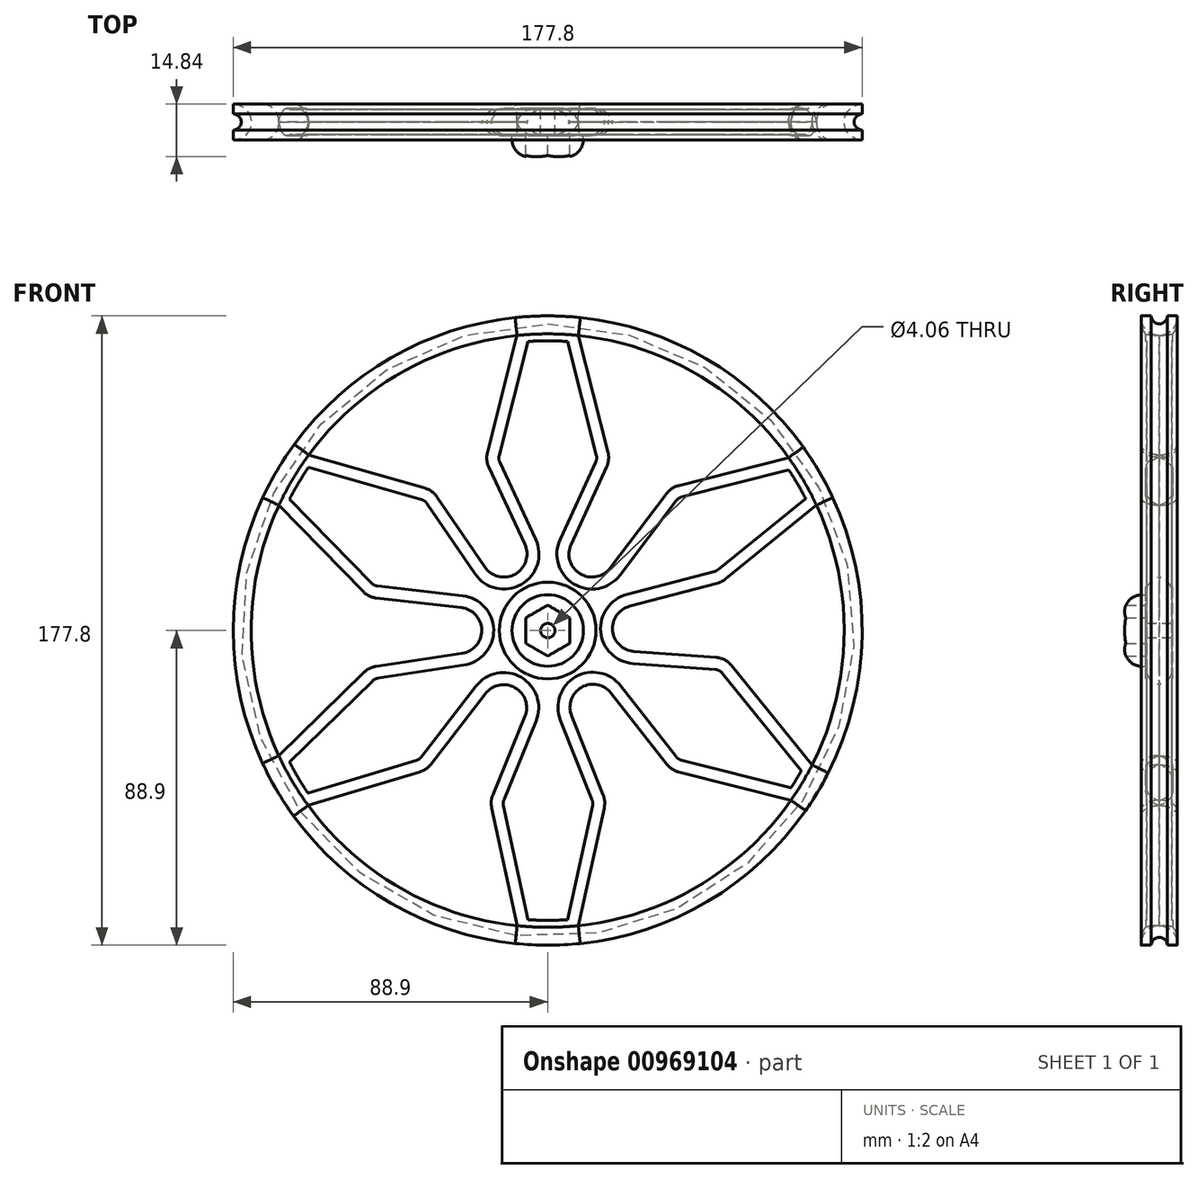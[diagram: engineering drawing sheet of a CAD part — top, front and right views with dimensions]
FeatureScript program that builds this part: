
annotation { "Feature Type Name" : "Feature", "Feature Type Description" : "" }
export const myFeature = defineFeature(function(context is Context, id is Id, definition is map)
    precondition{}
    {
        {
            var Q0;
            Q0=qCreatedBy(makeId("Top.planeOp"),FACE);
            var sketch = newSketch(context, id + "F0", { "sketchPlane" : qUnion([Q0])});
            skLineSegment(sketch, "E0", {"start": v(83.82, 0) * mm, "end": v(83.82, -5.08) * mm});
            skLineSegment(sketch, "E1", {"start": v(83.82, 0) * mm, "end": v(83.82, 5.08) * mm});
            skLineSegment(sketch, "E2", {"start": v(83.82, 5.08) * mm, "end": v(88.9, 5.08) * mm});
            skLineSegment(sketch, "E3", {"start": v(88.9, 5.08) * mm, "end": v(83.82, 5.08) * mm});
            skLineSegment(sketch, "E4", {"start": v(83.82, -5.08) * mm, "end": v(88.9, -5.08) * mm});
            skPoint(sketch, "E5.positionSnap0", {"position": v(83.82, 2.54) * mm});
            skPoint(sketch, "E6.positionSnap0", {"position": v(83.82, -2.54) * mm});
            skLineSegment(sketch, "E7", {"start": v(88.9, 3.88) * mm, "end": v(88.9, 5.08) * mm});
            skLineSegment(sketch, "E8", {"start": v(88.9, -5.08) * mm, "end": v(88.9, -3.83) * mm});
            skLineSegment(sketch, "E9", {"start": v(0, 0) * mm, "end": v(0, 19.3) * mm});
            skLineSegment(sketch, "E10", {"start": v(0, 19.3) * mm, "end": v(0, 0) * mm});
            skLineSegment(sketch, "E11", {"start": v(0, -18.69) * mm, "end": v(0, -1.26) * mm});
            skArc(sketch, "E12", {"start": v(88.9, 2.3) * mm, "mid": v(86.64, 0.03) * mm, "end": v(88.9, -2.25) * mm});
            skLineSegment(sketch, "E13", {"start": v(88.9, 2.3) * mm, "end": v(88.9, 3.88) * mm});
            skLineSegment(sketch, "E14", {"start": v(88.9, -2.25) * mm, "end": v(88.9, -3.83) * mm});
            skSolve(sketch);
        }
        {
            var Q0;
            Q0=makeQuery(id+"F0.imprint","IMPRINT",FACE,{"disambiguationData":[TD([[makeQuery(id+"F0.imprint","IMPRINT",EDGE,{"derivedFrom":sQuery(id+"F0.wireOp",EDGE,"E0")}),1.0]])]});
            var Q1;
            Q1=sQuery(id+"F0.wireOp",EDGE,"E11");
            var Q2;
            Q2=sQuery(id+"F0.wireOp",EDGE,"4J2hV2uY-nMCx-U5Xb-nDJS-bzSXFnuGIXOy");
            var Q3;
            Q3=sQuery(id+"F0.wireOp",EDGE,"E4");
            var Q4;
            Q4=sQuery(id+"F0.wireOp",EDGE,"E3");
            var Q5;
            Q5=sQuery(id+"F0.wireOp",EDGE,"E1");
            var Q6;
            Q6=sQuery(id+"F0.wireOp",EDGE,"E0");
            var Q7;
            Q7=sQuery(id+"F0.wireOp",EDGE,"E10");
            revolve(context, id + "F1", {"surfaceOperationType" : NewSurfaceOperationType.NEW, "entities" : qUnion([Q0]), "surfaceEntities" : qUnion([Q1, Q2, Q3, Q4, Q5, Q6]), "axis" : qUnion([Q7]), "revolveType" : RevolveType.FULL});
        }
        {
            var Q0;
            Q0=qCreatedBy(makeId("Front.planeOp"),FACE);
            var sketch = newSketch(context, id + "F2", { "sketchPlane" : qUnion([Q0])});
            skCircle(sketch, "E15", {"center": v(0, 0) * mm, "radius": 10.1 * mm});
            skLineSegment(sketch, "E16", {"start": v(-24.46, 6.34) * mm, "end": v(-48.48, 9.05) * mm});
            skLineSegment(sketch, "E17", {"start": v(-17.62, 18.03) * mm, "end": v(-31.2, 37.89) * mm});
            skLineSegment(sketch, "E18", {"start": v(6.74, 24.3) * mm, "end": v(16.82, 46.17) * mm});
            skLineSegment(sketch, "E19", {"start": v(-6.62, 24.3) * mm, "end": v(-16.8, 46.11) * mm});
            skLineSegment(sketch, "E20", {"start": v(17.57, 17.8) * mm, "end": v(33.5, 38.84) * mm});
            skLineSegment(sketch, "E21", {"start": v(23.23, 6.73) * mm, "end": v(48.04, 13.25) * mm});
            skLineSegment(sketch, "E22", {"start": v(24.38, -5.75) * mm, "end": v(47.6, -7.42) * mm});
            skLineSegment(sketch, "E23", {"start": v(17.82, -17.77) * mm, "end": v(33.5, -37.84) * mm});
            skLineSegment(sketch, "E24", {"start": v(6.92, -24.03) * mm, "end": v(15.83, -46.4) * mm});
            skLineSegment(sketch, "E25", {"start": v(-15.65, -46.4) * mm, "end": v(-6.58, -24.2) * mm});
            skLineSegment(sketch, "E26", {"start": v(-32.88, -37.86) * mm, "end": v(-17.48, -17.92) * mm});
            skLineSegment(sketch, "E27", {"start": v(-48.58, -9.96) * mm, "end": v(-24.22, -6.25) * mm});
            skCircle(sketch, "E28", {"center": v(0, 0) * mm, "radius": 85.43 * mm});
            skLineSegment(sketch, "E29", {"start": v(-17.2, 50.35) * mm, "end": v(-8.43, 85.01) * mm});
            skLineSegment(sketch, "E30", {"start": v(17.2, 50.39) * mm, "end": v(8.43, 85.01) * mm});
            skLineSegment(sketch, "E31", {"start": v(37, 41.16) * mm, "end": v(69.67, 49.44) * mm});
            skLineSegment(sketch, "E32", {"start": v(36.95, -40.08) * mm, "end": v(70.32, -48.51) * mm});
            skLineSegment(sketch, "E33", {"start": v(-34.7, 40.4) * mm, "end": v(-69.1, 50.24) * mm});
            skLineSegment(sketch, "E34", {"start": v(-52.3, 10.93) * mm, "end": v(-77.25, 36.47) * mm});
            skLineSegment(sketch, "E35", {"start": v(-52.06, -11.7) * mm, "end": v(-77.29, -36.4) * mm});
            skLineSegment(sketch, "E36", {"start": v(-36.08, -40.06) * mm, "end": v(-69.26, -50.02) * mm});
            skLineSegment(sketch, "E37", {"start": v(-15.98, -50.13) * mm, "end": v(-8.46, -85.01) * mm});
            skLineSegment(sketch, "E38", {"start": v(16.13, -50.11) * mm, "end": v(8.46, -85.01) * mm});
            skLineSegment(sketch, "E39", {"start": v(50.42, 14.47) * mm, "end": v(77.33, 36.32) * mm});
            skLineSegment(sketch, "E40", {"start": v(52.07, -9.75) * mm, "end": v(77.33, -40.86) * mm});
            skLineSegment(sketch, "E41", {"start": v(77.66, -35.6) * mm, "end": v(77.33, -40.86) * mm});
            skPoint(sketch, "E42.visualSharp", {"position": v(-50.73, 9.3) * mm});
            skArc(sketch, "E42.filletArc", {"start": v(-52.3, 10.93) * mm, "mid": v(-50.56, 9.66) * mm, "end": v(-48.48, 9.05) * mm});
            skPoint(sketch, "E43.visualSharp", {"position": v(-32.5, 39.78) * mm});
            skArc(sketch, "E43.filletArc", {"start": v(-31.2, 37.89) * mm, "mid": v(-32.73, 39.45) * mm, "end": v(-34.7, 40.4) * mm});
            skPoint(sketch, "E44.visualSharp", {"position": v(-50.6, -10.27) * mm});
            skArc(sketch, "E44.filletArc", {"start": v(-48.58, -9.96) * mm, "mid": v(-50.46, -10.55) * mm, "end": v(-52.06, -11.7) * mm});
            skPoint(sketch, "E45.visualSharp", {"position": v(-34.12, -39.47) * mm});
            skArc(sketch, "E45.filletArc", {"start": v(-36.08, -40.06) * mm, "mid": v(-34.3, -39.2) * mm, "end": v(-32.88, -37.86) * mm});
            skPoint(sketch, "E46.visualSharp", {"position": v(-17.75, 48.16) * mm});
            skArc(sketch, "E46.filletArc", {"start": v(-17.2, 50.35) * mm, "mid": v(-17.36, 48.2) * mm, "end": v(-16.8, 46.11) * mm});
            skPoint(sketch, "E47.visualSharp", {"position": v(17.75, 48.21) * mm});
            skArc(sketch, "E47.filletArc", {"start": v(16.82, 46.17) * mm, "mid": v(17.37, 48.25) * mm, "end": v(17.2, 50.39) * mm});
            skPoint(sketch, "E48.visualSharp", {"position": v(34.84, 40.61) * mm});
            skArc(sketch, "E48.filletArc", {"start": v(37, 41.16) * mm, "mid": v(35.05, 40.3) * mm, "end": v(33.5, 38.84) * mm});
            skPoint(sketch, "E49.visualSharp", {"position": v(49.36, 13.6) * mm});
            skArc(sketch, "E49.filletArc", {"start": v(48.04, 13.25) * mm, "mid": v(49.3, 13.73) * mm, "end": v(50.42, 14.47) * mm});
            skPoint(sketch, "E50.visualSharp", {"position": v(50.34, -7.62) * mm});
            skArc(sketch, "E50.filletArc", {"start": v(52.07, -9.75) * mm, "mid": v(50.07, -8.13) * mm, "end": v(47.6, -7.42) * mm});
            skPoint(sketch, "E51.visualSharp", {"position": v(34.84, -39.55) * mm});
            skArc(sketch, "E51.filletArc", {"start": v(33.5, -37.84) * mm, "mid": v(35.04, -39.25) * mm, "end": v(36.95, -40.08) * mm});
            skPoint(sketch, "E52.visualSharp", {"position": v(16.55, -48.21) * mm});
            skArc(sketch, "E52.filletArc", {"start": v(16.13, -50.11) * mm, "mid": v(16.26, -48.23) * mm, "end": v(15.83, -46.4) * mm});
            skPoint(sketch, "E53.visualSharp", {"position": v(-16.4, -48.21) * mm});
            skArc(sketch, "E53.filletArc", {"start": v(-15.65, -46.4) * mm, "mid": v(-16.1, -48.24) * mm, "end": v(-15.98, -50.13) * mm});
            skPoint(sketch, "E54.endSnap0", {"position": v(25.3, 7.3) * mm});
            skArc(sketch, "E55.filletArc", {"start": v(-6.58, -24.2) * mm, "mid": v(-9.28, -16.3) * mm, "end": v(-17.48, -17.92) * mm});
            skArc(sketch, "E56.filletArc", {"start": v(17.82, -17.77) * mm, "mid": v(9.66, -16.18) * mm, "end": v(6.92, -24.03) * mm});
            skArc(sketch, "E57.filletArc", {"start": v(23.23, 6.73) * mm, "mid": v(18.52, 0) * mm, "end": v(24.38, -5.75) * mm});
            skArc(sketch, "E58.filletArc", {"start": v(6.74, 24.3) * mm, "mid": v(9.25, 16.2) * mm, "end": v(17.57, 17.8) * mm});
            skArc(sketch, "E59.filletArc", {"start": v(-17.62, 18.03) * mm, "mid": v(-9.23, 16.1) * mm, "end": v(-6.62, 24.3) * mm});
            skArc(sketch, "E60.filletArc", {"start": v(-24.22, -6.25) * mm, "mid": v(-18.82, 0.15) * mm, "end": v(-24.46, 6.34) * mm});
            skPoint(sketch, "E61.startSnap0", {"position": v(18.52, 0) * mm});
            skCircle(sketch, "E62", {"center": v(0, 0) * mm, "radius": 2.03 * mm});
            skLineSegment(sketch, "E63.0", {"start": v(0, -7.19) * mm, "end": v(-6.22, -3.6) * mm});
            skLineSegment(sketch, "E63.1", {"start": v(-6.22, -3.6) * mm, "end": v(-6.22, 3.6) * mm});
            skLineSegment(sketch, "E63.2", {"start": v(-6.22, 3.6) * mm, "end": v(0, 7.19) * mm});
            skLineSegment(sketch, "E63.3", {"start": v(0, 7.19) * mm, "end": v(6.22, 3.6) * mm});
            skLineSegment(sketch, "E63.4", {"start": v(6.22, 3.6) * mm, "end": v(6.22, -3.6) * mm});
            skLineSegment(sketch, "E63.5", {"start": v(6.22, -3.6) * mm, "end": v(0, -7.19) * mm});
            skSolve(sketch);
        }
        {
            var Q0;
            Q0=makeQuery(id+"F2.imprint","IMPRINT",FACE,{"disambiguationData":[TD([[makeQuery(id+"F2.imprint","IMPRINT",EDGE,{"derivedFrom":sQuery(id+"F2.wireOp",EDGE,"E18")}),1.0]])]});
            var Q1;
            Q1=makeQuery(id+"F2.imprint","IMPRINT",FACE,{"disambiguationData":[TD([[makeQuery(id+"F2.imprint","IMPRINT",EDGE,{"derivedFrom":sQuery(id+"F2.wireOp",EDGE,"E20")}),-1.0]])]});
            var Q2;
            Q2=makeQuery(id+"F2.imprint","IMPRINT",FACE,{"disambiguationData":[TD([[makeQuery(id+"F2.imprint","IMPRINT",EDGE,{"derivedFrom":sQuery(id+"F2.wireOp",EDGE,"E22")}),-1.0]])]});
            var Q3;
            Q3=makeQuery(id+"F2.imprint","IMPRINT",FACE,{"disambiguationData":[TD([[makeQuery(id+"F2.imprint","IMPRINT",EDGE,{"derivedFrom":sQuery(id+"F2.wireOp",EDGE,"E24")}),-1.0]])]});
            var Q4;
            Q4=makeQuery(id+"F2.imprint","IMPRINT",FACE,{"disambiguationData":[TD([[makeQuery(id+"F2.imprint","IMPRINT",EDGE,{"derivedFrom":sQuery(id+"F2.wireOp",EDGE,"E26")}),1.0]])]});
            var Q5;
            Q5=makeQuery(id+"F2.imprint","IMPRINT",FACE,{"disambiguationData":[TD([[makeQuery(id+"F2.imprint","IMPRINT",EDGE,{"derivedFrom":sQuery(id+"F2.wireOp",EDGE,"E16")}),-1.0]])]});
            var Q6;
            Q6=makeQuery(id+"F2.imprint","IMPRINT",FACE,{"disambiguationData":[TD([[makeQuery(id+"F2.imprint","IMPRINT",EDGE,{"derivedFrom":sQuery(id+"F2.wireOp",EDGE,"c844d40d-d56d-44c7-8cb0-b91d600c20de.0")}),-1.0]])]});
            var Q7;
            Q7=makeQuery(id+"F2.imprint","IMPRINT",FACE,{"disambiguationData":[TD([[makeQuery(id+"F2.imprint","IMPRINT",EDGE,{"derivedFrom":sQuery(id+"F2.wireOp",EDGE,"E62")}),-1.0]])]});
            extrude(context, id + "F3", {"entities" : qUnion([Q0, Q1, Q2, Q3, Q4, Q5, Q6, Q7]), "depth" : 3.8 * mm, "offsetDistance" : 25.4 * mm});
        }
        {
            var Q0;
            Q0=makeQuery(id+"F3.opExtrude","CAP_FACE",FACE,{"disambiguationData":[OSD([sQuery(id+"F2.wireOp",EDGE,"E16"),sQuery(id+"F2.wireOp",EDGE,"E17"),sQuery(id+"F2.wireOp",EDGE,"E28"),sQuery(id+"F2.wireOp",EDGE,"E33"),sQuery(id+"F2.wireOp",EDGE,"E34"),sQuery(id+"F2.wireOp",EDGE,"E42.filletArc"),sQuery(id+"F2.wireOp",EDGE,"E43.filletArc")])],"isStart":false});
            var Q1;
            Q1=makeQuery(id+"F3.opExtrude","CAP_FACE",FACE,{"disambiguationData":[OSD([sQuery(id+"F2.wireOp",EDGE,"E18"),sQuery(id+"F2.wireOp",EDGE,"E19"),sQuery(id+"F2.wireOp",EDGE,"E28"),sQuery(id+"F2.wireOp",EDGE,"E29"),sQuery(id+"F2.wireOp",EDGE,"E30"),sQuery(id+"F2.wireOp",EDGE,"E46.filletArc"),sQuery(id+"F2.wireOp",EDGE,"E47.filletArc")])],"isStart":false});
            var Q2;
            Q2=makeQuery(id+"F3.opExtrude","CAP_FACE",FACE,{"disambiguationData":[OSD([sQuery(id+"F2.wireOp",EDGE,"E20"),sQuery(id+"F2.wireOp",EDGE,"E21"),sQuery(id+"F2.wireOp",EDGE,"E28"),sQuery(id+"F2.wireOp",EDGE,"E31"),sQuery(id+"F2.wireOp",EDGE,"E39"),sQuery(id+"F2.wireOp",EDGE,"E48.filletArc"),sQuery(id+"F2.wireOp",EDGE,"E49.filletArc")])],"isStart":false});
            var Q3;
            Q3=makeQuery(id+"F3.opExtrude","CAP_FACE",FACE,{"disambiguationData":[OSD([sQuery(id+"F2.wireOp",EDGE,"E22"),sQuery(id+"F2.wireOp",EDGE,"E23"),sQuery(id+"F2.wireOp",EDGE,"E28"),sQuery(id+"F2.wireOp",EDGE,"E32"),sQuery(id+"F2.wireOp",EDGE,"E40"),sQuery(id+"F2.wireOp",EDGE,"E41"),sQuery(id+"F2.wireOp",EDGE,"E50.filletArc"),sQuery(id+"F2.wireOp",EDGE,"E51.filletArc")])],"isStart":false});
            var Q4;
            Q4=makeQuery(id+"F3.opExtrude","CAP_FACE",FACE,{"disambiguationData":[OSD([sQuery(id+"F2.wireOp",EDGE,"E24"),sQuery(id+"F2.wireOp",EDGE,"E25"),sQuery(id+"F2.wireOp",EDGE,"E28"),sQuery(id+"F2.wireOp",EDGE,"E37"),sQuery(id+"F2.wireOp",EDGE,"E38"),sQuery(id+"F2.wireOp",EDGE,"E52.filletArc"),sQuery(id+"F2.wireOp",EDGE,"E53.filletArc")])],"isStart":false});
            var Q5;
            Q5=makeQuery(id+"F3.opExtrude","CAP_FACE",FACE,{"disambiguationData":[OSD([sQuery(id+"F2.wireOp",EDGE,"E26"),sQuery(id+"F2.wireOp",EDGE,"E27"),sQuery(id+"F2.wireOp",EDGE,"E28"),sQuery(id+"F2.wireOp",EDGE,"E35"),sQuery(id+"F2.wireOp",EDGE,"E36"),sQuery(id+"F2.wireOp",EDGE,"E44.filletArc"),sQuery(id+"F2.wireOp",EDGE,"E45.filletArc")])],"isStart":false});
            shell(context, id + "F4", {"entities" : qUnion([Q0, Q1, Q2, Q3, Q4, Q5]), "thickness" : 3.56 * mm});
        }
        {
            var Q0;
            Q0=makeQuery(id+"F3.opExtrude","SWEPT_BODY",BODY,{"disambiguationData":[OSD([sQuery(id+"F2.wireOp",EDGE,"E20"),sQuery(id+"F2.wireOp",EDGE,"E21"),sQuery(id+"F2.wireOp",EDGE,"E28"),sQuery(id+"F2.wireOp",EDGE,"E31"),sQuery(id+"F2.wireOp",EDGE,"E39")])]});
            var Q1;
            Q1=makeQuery(id+"F3.opExtrude","SWEPT_BODY",BODY,{"disambiguationData":[OSD([sQuery(id+"F2.wireOp",EDGE,"E22"),sQuery(id+"F2.wireOp",EDGE,"E23"),sQuery(id+"F2.wireOp",EDGE,"E28"),sQuery(id+"F2.wireOp",EDGE,"E32"),sQuery(id+"F2.wireOp",EDGE,"E40"),sQuery(id+"F2.wireOp",EDGE,"E41")])]});
            var Q2;
            Q2=makeQuery(id+"F3.opExtrude","SWEPT_BODY",BODY,{"disambiguationData":[OSD([sQuery(id+"F2.wireOp",EDGE,"E24"),sQuery(id+"F2.wireOp",EDGE,"E25"),sQuery(id+"F2.wireOp",EDGE,"E28"),sQuery(id+"F2.wireOp",EDGE,"E37"),sQuery(id+"F2.wireOp",EDGE,"E38")])]});
            var Q3;
            Q3=makeQuery(id+"F3.opExtrude","SWEPT_BODY",BODY,{"disambiguationData":[OSD([sQuery(id+"F2.wireOp",EDGE,"E26"),sQuery(id+"F2.wireOp",EDGE,"E27"),sQuery(id+"F2.wireOp",EDGE,"E28"),sQuery(id+"F2.wireOp",EDGE,"E35"),sQuery(id+"F2.wireOp",EDGE,"E36")])]});
            var Q4;
            Q4=makeQuery(id+"F3.opExtrude","SWEPT_BODY",BODY,{"disambiguationData":[OSD([sQuery(id+"F2.wireOp",EDGE,"c844d40d-d56d-44c7-8cb0-b91d600c20de.0"),sQuery(id+"F2.wireOp",EDGE,"c844d40d-d56d-44c7-8cb0-b91d600c20de.1"),sQuery(id+"F2.wireOp",EDGE,"c844d40d-d56d-44c7-8cb0-b91d600c20de.2"),sQuery(id+"F2.wireOp",EDGE,"c844d40d-d56d-44c7-8cb0-b91d600c20de.3"),sQuery(id+"F2.wireOp",EDGE,"c844d40d-d56d-44c7-8cb0-b91d600c20de.4"),sQuery(id+"F2.wireOp",EDGE,"c844d40d-d56d-44c7-8cb0-b91d600c20de.5")])]});
            var Q5;
            Q5=makeQuery(id+"F3.opExtrude","SWEPT_BODY",BODY,{"disambiguationData":[OSD([sQuery(id+"F2.wireOp",EDGE,"E16"),sQuery(id+"F2.wireOp",EDGE,"E17"),sQuery(id+"F2.wireOp",EDGE,"E28"),sQuery(id+"F2.wireOp",EDGE,"E33"),sQuery(id+"F2.wireOp",EDGE,"E34")])]});
            var Q6;
            Q6=makeQuery(id+"F3.opExtrude","SWEPT_BODY",BODY,{"disambiguationData":[OSD([sQuery(id+"F2.wireOp",EDGE,"E18"),sQuery(id+"F2.wireOp",EDGE,"E19"),sQuery(id+"F2.wireOp",EDGE,"E28"),sQuery(id+"F2.wireOp",EDGE,"E29"),sQuery(id+"F2.wireOp",EDGE,"E30")])]});
            var Q7;
            Q7=makeQuery(id+"FEBJNoevQ1nLVfz_7.opExtrude","SWEPT_BODY",BODY,{"disambiguationData":[OSD([sQuery(id+"F2.wireOp",EDGE,"c844d40d-d56d-44c7-8cb0-b91d600c20de.0"),sQuery(id+"F2.wireOp",EDGE,"c844d40d-d56d-44c7-8cb0-b91d600c20de.1"),sQuery(id+"F2.wireOp",EDGE,"c844d40d-d56d-44c7-8cb0-b91d600c20de.2"),sQuery(id+"F2.wireOp",EDGE,"c844d40d-d56d-44c7-8cb0-b91d600c20de.3"),sQuery(id+"F2.wireOp",EDGE,"c844d40d-d56d-44c7-8cb0-b91d600c20de.4"),sQuery(id+"F2.wireOp",EDGE,"c844d40d-d56d-44c7-8cb0-b91d600c20de.5")])]});
            var Q8;
            Q8=qCreatedBy(makeId("Front.planeOp"),FACE);
            mirror(context, id + "F5", {"entities" : qUnion([Q0, Q1, Q2, Q3, Q4, Q5, Q6, Q7]), "mirrorPlane" : qUnion([Q8])});
        }
        {
            var Q0;
            Q0=makeQuery(id+"F2.imprint","IMPRINT",FACE,{"disambiguationData":[TD([[makeQuery(id+"F2.imprint","IMPRINT",EDGE,{"derivedFrom":sQuery(id+"F2.wireOp",EDGE,"E15")}),1.0]])]});
            extrude(context, id + "F6", {"entities" : qUnion([Q0]), "depth" : 9.9 * mm, "offsetDistance" : 25.4 * mm});
        }
        {
            var Q0;
            Q0=makeQuery(id+"F2.imprint","IMPRINT",FACE,{"disambiguationData":[TD([[makeQuery(id+"F2.imprint","IMPRINT",EDGE,{"derivedFrom":sQuery(id+"F2.wireOp",EDGE,"E62")}),-1.0]])]});
            var Q1;
            Q1=makeQuery(id+"F2.imprint","IMPRINT",FACE,{"disambiguationData":[TD([[makeQuery(id+"F2.imprint","IMPRINT",EDGE,{"derivedFrom":sQuery(id+"F2.wireOp",EDGE,"E15")}),1.0]])]});
            extrude(context, id + "F7", {"entities" : qUnion([Q0, Q1]), "oppositeDirection" : true, "depth" : 3.8 * mm, "offsetDistance" : 25.4 * mm});
        }
        {
            var Q0;
            Q0=makeQuery(id+"F3.opExtrude","SWEPT_BODY",BODY,{"disambiguationData":[OSD([sQuery(id+"F2.wireOp",EDGE,"E15"),sQuery(id+"F2.wireOp",EDGE,"E16"),sQuery(id+"F2.wireOp",EDGE,"E17"),sQuery(id+"F2.wireOp",EDGE,"E18"),sQuery(id+"F2.wireOp",EDGE,"E19"),sQuery(id+"F2.wireOp",EDGE,"E20"),sQuery(id+"F2.wireOp",EDGE,"E21"),sQuery(id+"F2.wireOp",EDGE,"E22"),sQuery(id+"F2.wireOp",EDGE,"E23"),sQuery(id+"F2.wireOp",EDGE,"E24"),sQuery(id+"F2.wireOp",EDGE,"E25"),sQuery(id+"F2.wireOp",EDGE,"E26"),sQuery(id+"F2.wireOp",EDGE,"E27"),sQuery(id+"F2.wireOp",EDGE,"E28"),sQuery(id+"F2.wireOp",EDGE,"E29"),sQuery(id+"F2.wireOp",EDGE,"E30"),sQuery(id+"F2.wireOp",EDGE,"E31"),sQuery(id+"F2.wireOp",EDGE,"E32"),sQuery(id+"F2.wireOp",EDGE,"E33"),sQuery(id+"F2.wireOp",EDGE,"E34"),sQuery(id+"F2.wireOp",EDGE,"E35"),sQuery(id+"F2.wireOp",EDGE,"E36"),sQuery(id+"F2.wireOp",EDGE,"E37"),sQuery(id+"F2.wireOp",EDGE,"E38"),sQuery(id+"F2.wireOp",EDGE,"E39"),sQuery(id+"F2.wireOp",EDGE,"E40"),sQuery(id+"F2.wireOp",EDGE,"E42.filletArc"),sQuery(id+"F2.wireOp",EDGE,"E43.filletArc"),sQuery(id+"F2.wireOp",EDGE,"E44.filletArc"),sQuery(id+"F2.wireOp",EDGE,"E45.filletArc"),sQuery(id+"F2.wireOp",EDGE,"E46.filletArc"),sQuery(id+"F2.wireOp",EDGE,"E47.filletArc"),sQuery(id+"F2.wireOp",EDGE,"E48.filletArc"),sQuery(id+"F2.wireOp",EDGE,"E49.filletArc"),sQuery(id+"F2.wireOp",EDGE,"E50.filletArc"),sQuery(id+"F2.wireOp",EDGE,"E51.filletArc"),sQuery(id+"F2.wireOp",EDGE,"E52.filletArc"),sQuery(id+"F2.wireOp",EDGE,"E53.filletArc"),sQuery(id+"F2.wireOp",EDGE,"E55.filletArc"),sQuery(id+"F2.wireOp",EDGE,"E56.filletArc"),sQuery(id+"F2.wireOp",EDGE,"E57.filletArc"),sQuery(id+"F2.wireOp",EDGE,"E58.filletArc"),sQuery(id+"F2.wireOp",EDGE,"E59.filletArc"),sQuery(id+"F2.wireOp",EDGE,"E60.filletArc")])]});
            var Q1;
            Q1=makeQuery(id+"F3.opExtrude","SWEPT_BODY",BODY,{"disambiguationData":[OSD([sQuery(id+"F2.wireOp",EDGE,"E62"),sQuery(id+"F2.wireOp",EDGE,"E63.0"),sQuery(id+"F2.wireOp",EDGE,"E63.1"),sQuery(id+"F2.wireOp",EDGE,"E63.2"),sQuery(id+"F2.wireOp",EDGE,"E63.3"),sQuery(id+"F2.wireOp",EDGE,"E63.4"),sQuery(id+"F2.wireOp",EDGE,"E63.5")])]});
            var Q2;
            Q2=makeQuery(id+"F5.opPattern","COPY",BODY,{"derivedFrom":makeQuery(id+"F3.opExtrude","SWEPT_BODY",BODY,{"disambiguationData":[OSD([sQuery(id+"F2.wireOp",EDGE,"E15"),sQuery(id+"F2.wireOp",EDGE,"E16"),sQuery(id+"F2.wireOp",EDGE,"E17"),sQuery(id+"F2.wireOp",EDGE,"E18"),sQuery(id+"F2.wireOp",EDGE,"E19"),sQuery(id+"F2.wireOp",EDGE,"E20"),sQuery(id+"F2.wireOp",EDGE,"E21"),sQuery(id+"F2.wireOp",EDGE,"E22"),sQuery(id+"F2.wireOp",EDGE,"E23"),sQuery(id+"F2.wireOp",EDGE,"E24"),sQuery(id+"F2.wireOp",EDGE,"E25"),sQuery(id+"F2.wireOp",EDGE,"E26"),sQuery(id+"F2.wireOp",EDGE,"E27"),sQuery(id+"F2.wireOp",EDGE,"E28"),sQuery(id+"F2.wireOp",EDGE,"E29"),sQuery(id+"F2.wireOp",EDGE,"E30"),sQuery(id+"F2.wireOp",EDGE,"E31"),sQuery(id+"F2.wireOp",EDGE,"E32"),sQuery(id+"F2.wireOp",EDGE,"E33"),sQuery(id+"F2.wireOp",EDGE,"E34"),sQuery(id+"F2.wireOp",EDGE,"E35"),sQuery(id+"F2.wireOp",EDGE,"E36"),sQuery(id+"F2.wireOp",EDGE,"E37"),sQuery(id+"F2.wireOp",EDGE,"E38"),sQuery(id+"F2.wireOp",EDGE,"E39"),sQuery(id+"F2.wireOp",EDGE,"E40"),sQuery(id+"F2.wireOp",EDGE,"E42.filletArc"),sQuery(id+"F2.wireOp",EDGE,"E43.filletArc"),sQuery(id+"F2.wireOp",EDGE,"E44.filletArc"),sQuery(id+"F2.wireOp",EDGE,"E45.filletArc"),sQuery(id+"F2.wireOp",EDGE,"E46.filletArc"),sQuery(id+"F2.wireOp",EDGE,"E47.filletArc"),sQuery(id+"F2.wireOp",EDGE,"E48.filletArc"),sQuery(id+"F2.wireOp",EDGE,"E49.filletArc"),sQuery(id+"F2.wireOp",EDGE,"E50.filletArc"),sQuery(id+"F2.wireOp",EDGE,"E51.filletArc"),sQuery(id+"F2.wireOp",EDGE,"E52.filletArc"),sQuery(id+"F2.wireOp",EDGE,"E53.filletArc"),sQuery(id+"F2.wireOp",EDGE,"E55.filletArc"),sQuery(id+"F2.wireOp",EDGE,"E56.filletArc"),sQuery(id+"F2.wireOp",EDGE,"E57.filletArc"),sQuery(id+"F2.wireOp",EDGE,"E58.filletArc"),sQuery(id+"F2.wireOp",EDGE,"E59.filletArc"),sQuery(id+"F2.wireOp",EDGE,"E60.filletArc")])]}),"instanceName":"1"});
            var Q3;
            Q3=makeQuery(id+"F6.opExtrude","SWEPT_BODY",BODY,{"disambiguationData":[OSD([sQuery(id+"F2.wireOp",EDGE,"E15"),sQuery(id+"F2.wireOp",EDGE,"E63.0"),sQuery(id+"F2.wireOp",EDGE,"E63.1"),sQuery(id+"F2.wireOp",EDGE,"E63.2"),sQuery(id+"F2.wireOp",EDGE,"E63.3"),sQuery(id+"F2.wireOp",EDGE,"E63.4"),sQuery(id+"F2.wireOp",EDGE,"E63.5")])]});
            var Q4;
            Q4=makeQuery(id+"F7.opExtrude","SWEPT_BODY",BODY,{"disambiguationData":[OSD([sQuery(id+"F2.wireOp",EDGE,"E15"),sQuery(id+"F2.wireOp",EDGE,"E62")])]});
            var Q5;
            Q5=makeQuery(id+"F1.opRevolve","SWEPT_BODY",BODY,{"disambiguationData":[OSD([sQuery(id+"F0.wireOp",EDGE,"E0"),sQuery(id+"F0.wireOp",EDGE,"E1"),sQuery(id+"F0.wireOp",EDGE,"E3"),sQuery(id+"F0.wireOp",EDGE,"E4"),sQuery(id+"F0.wireOp",EDGE,"E7"),sQuery(id+"F0.wireOp",EDGE,"E8"),sQuery(id+"F0.wireOp",EDGE,"E12"),sQuery(id+"F0.wireOp",EDGE,"E13"),sQuery(id+"F0.wireOp",EDGE,"E14")])]});
            booleanBodies(context, id + "F8", {"operationType" : BooleanOperationType.UNION, "tools" : qUnion([Q0, Q1, Q2, Q3, Q4, Q5])});
        }
        {
            var Q0;
            {var subQ0=makeQuery(id+"F3.opExtrude","SWEPT_FACE",FACE,{"disambiguationData":[OSD([sQuery(id+"F2.wireOp",EDGE,"E19")])]});Q0=makeQuery(id+"F8.opBoolean","MERGE",FACE,{"derivedFrom":[subQ0,makeQuery(id+"F5.opPattern","COPY",FACE,{"derivedFrom":subQ0,"instanceName":"1"})]});}
            var Q1;
            Q1=makeQuery(id+"F3.opExtrude","CAP_EDGE",EDGE,{"disambiguationData":[OSD([sQuery(id+"F2.wireOp",EDGE,"E18")])],"isStart":false});
            var Q2;
            Q2=makeQuery(id+"F3.opExtrude","CAP_EDGE",EDGE,{"disambiguationData":[OSD([sQuery(id+"F2.wireOp",EDGE,"E21")])],"isStart":false});
            var Q3;
            Q3=makeQuery(id+"F3.opExtrude","CAP_EDGE",EDGE,{"disambiguationData":[OSD([sQuery(id+"F2.wireOp",EDGE,"E23")])],"isStart":false});
            var Q4;
            Q4=makeQuery(id+"F3.opExtrude","CAP_EDGE",EDGE,{"disambiguationData":[OSD([sQuery(id+"F2.wireOp",EDGE,"E25")])],"isStart":false});
            var Q5;
            Q5=makeQuery(id+"F3.opExtrude","CAP_EDGE",EDGE,{"disambiguationData":[OSD([sQuery(id+"F2.wireOp",EDGE,"E27")])],"isStart":false});
            var Q6;
            Q6=makeQuery(id+"F5.opPattern","COPY",EDGE,{"derivedFrom":makeQuery(id+"F3.opExtrude","CAP_EDGE",EDGE,{"disambiguationData":[OSD([sQuery(id+"F2.wireOp",EDGE,"E16")])],"isStart":false}),"instanceName":"1"});
            var Q7;
            Q7=makeQuery(id+"F5.opPattern","COPY",EDGE,{"derivedFrom":makeQuery(id+"F3.opExtrude","CAP_EDGE",EDGE,{"disambiguationData":[OSD([sQuery(id+"F2.wireOp",EDGE,"E26")])],"isStart":false}),"instanceName":"1"});
            var Q8;
            Q8=makeQuery(id+"F5.opPattern","COPY",EDGE,{"derivedFrom":makeQuery(id+"F3.opExtrude","CAP_EDGE",EDGE,{"disambiguationData":[OSD([sQuery(id+"F2.wireOp",EDGE,"E24")])],"isStart":false}),"instanceName":"1"});
            var Q9;
            Q9=makeQuery(id+"F5.opPattern","COPY",EDGE,{"derivedFrom":makeQuery(id+"F3.opExtrude","CAP_EDGE",EDGE,{"disambiguationData":[OSD([sQuery(id+"F2.wireOp",EDGE,"E22")])],"isStart":false}),"instanceName":"1"});
            var Q10;
            Q10=makeQuery(id+"F5.opPattern","COPY",EDGE,{"derivedFrom":makeQuery(id+"F3.opExtrude","CAP_EDGE",EDGE,{"disambiguationData":[OSD([sQuery(id+"F2.wireOp",EDGE,"E20")])],"isStart":false}),"instanceName":"1"});
            fillet(context, id + "F9", {"entities" : qUnion([Q0, Q1, Q2, Q3, Q4, Q5, Q6, Q7, Q8, Q9, Q10]), "radius" : 5.08 * mm, "tangentPropagation" : true, "allowEdgeOverflow" : false});
        }
        {
            var Q0;
            Q0=makeQuery(id+"F6.opExtrude","CAP_EDGE",EDGE,{"disambiguationData":[OSD([sQuery(id+"F2.wireOp",EDGE,"E15")])],"isStart":false});
            fillet(context, id + "F10", {"entities" : qUnion([Q0]), "radius" : 5.08 * mm, "tangentPropagation" : true, "allowEdgeOverflow" : false});
        }
        {
            var Q0;
            Q0=makeQuery(id+"F1.opRevolve","SWEPT_EDGE",EDGE,{"disambiguationData":[OSD([sQuery(id+"F0.wireOp",EDGE,"E0"),sQuery(id+"F0.wireOp",EDGE,"E4")])]});
            var Q1;
            Q1=makeQuery(id+"F1.opRevolve","SWEPT_EDGE",EDGE,{"disambiguationData":[OSD([sQuery(id+"F0.wireOp",EDGE,"E1"),sQuery(id+"F0.wireOp",EDGE,"E3")])]});
            fillet(context, id + "F11", {"entities" : qUnion([Q0, Q1]), "radius" : 5.08 * mm, "tangentPropagation" : true, "allowEdgeOverflow" : false});
        }
    });
